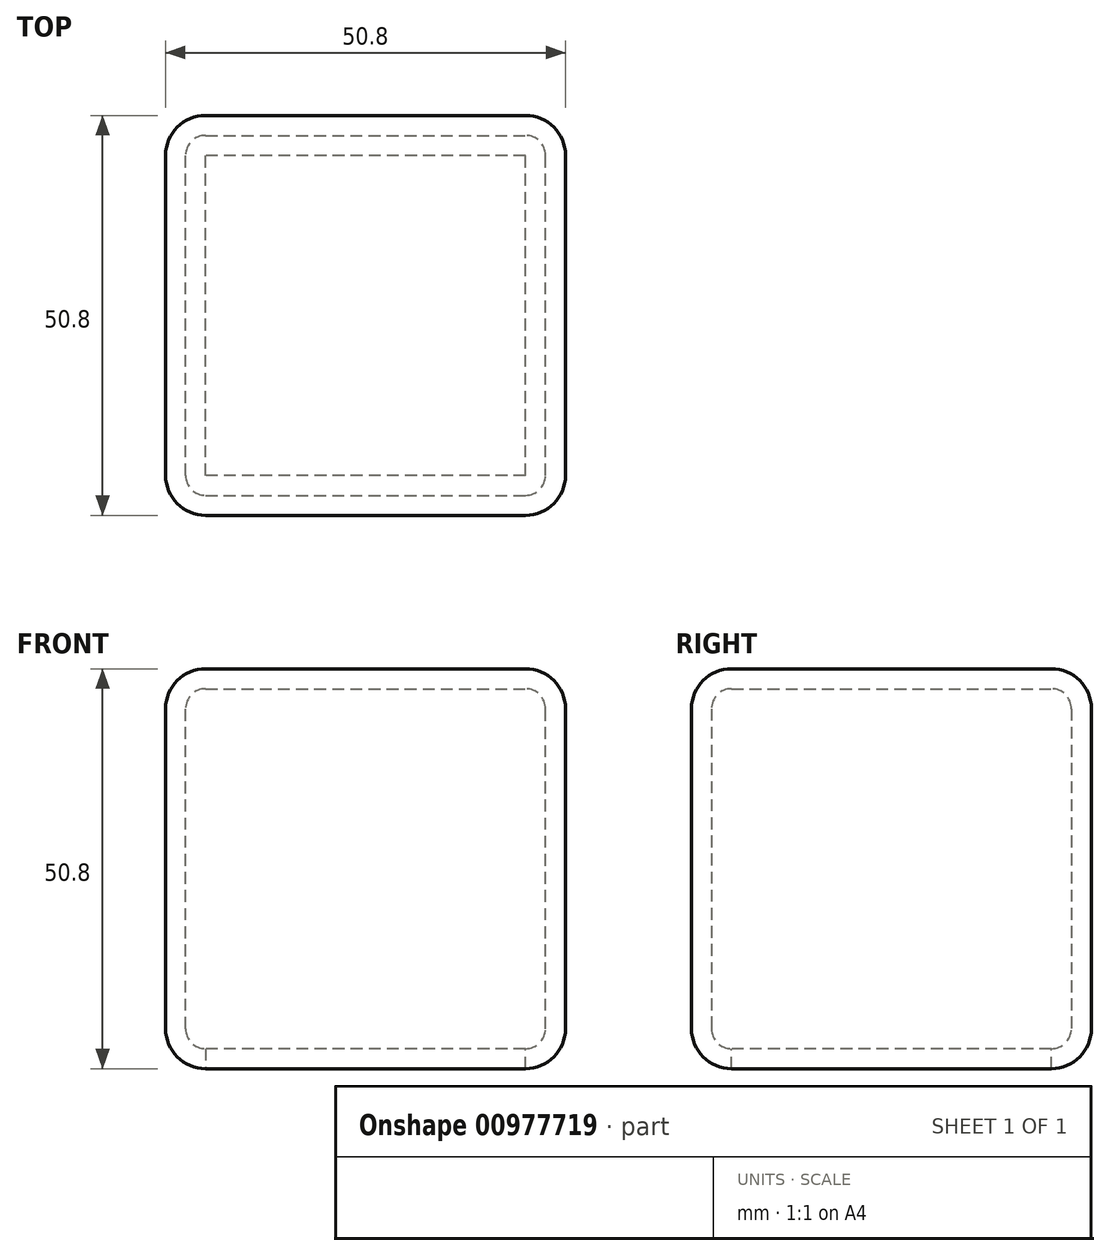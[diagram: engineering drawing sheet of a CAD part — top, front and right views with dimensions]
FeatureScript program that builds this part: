
annotation { "Feature Type Name" : "Feature", "Feature Type Description" : "" }
export const myFeature = defineFeature(function(context is Context, id is Id, definition is map)
    precondition{}
    {
        {
            var Q0;
            Q0=qCreatedBy(makeId("Top.planeOp"),FACE);
            var sketch = newSketch(context, id + "F0", { "sketchPlane" : qUnion([Q0])});
            skLineSegment(sketch, "E0.bottom", {"start": v(25.4, -25.4) * mm, "end": v(-25.4, -25.4) * mm});
            skLineSegment(sketch, "E0.top", {"start": v(25.4, 25.4) * mm, "end": v(-25.4, 25.4) * mm});
            skLineSegment(sketch, "E0.left", {"start": v(25.4, -25.4) * mm, "end": v(25.4, 25.4) * mm});
            skLineSegment(sketch, "E0.right", {"start": v(-25.4, -25.4) * mm, "end": v(-25.4, 25.4) * mm});
            skPoint(sketch, "E0.middle", {"position": v(0, 0) * mm});
            skSolve(sketch);
        }
        {
            var Q0;
            Q0=makeQuery(id+"F0.imprint","IMPRINT",FACE,{"disambiguationData":[TD([[makeQuery(id+"F0.imprint","IMPRINT",EDGE,{"derivedFrom":sQuery(id+"F0.wireOp",EDGE,"E0.bottom")}),-1.0]])]});
            extrude(context, id + "F1", {"entities" : qUnion([Q0]), "depth" : 50.8 * mm, "offsetDistance" : 25.4 * mm});
        }
        {
            var Q0;
            Q0=makeQuery(id+"F1.opExtrude","CAP_EDGE",EDGE,{"disambiguationData":[OSD([sQuery(id+"F0.wireOp",EDGE,"E0.right")])],"isStart":true});
            var Q1;
            Q1=makeQuery(id+"F1.opExtrude","CAP_EDGE",EDGE,{"disambiguationData":[OSD([sQuery(id+"F0.wireOp",EDGE,"E0.right")])],"isStart":false});
            var Q2;
            Q2=makeQuery(id+"F1.opExtrude","SWEPT_EDGE",EDGE,{"disambiguationData":[OSD([sQuery(id+"F0.wireOp",EDGE,"E0.top"),sQuery(id+"F0.wireOp",EDGE,"E0.right")])]});
            var Q3;
            Q3=makeQuery(id+"F1.opExtrude","CAP_EDGE",EDGE,{"disambiguationData":[OSD([sQuery(id+"F0.wireOp",EDGE,"E0.left")])],"isStart":false});
            var Q4;
            Q4=makeQuery(id+"F1.opExtrude","CAP_EDGE",EDGE,{"disambiguationData":[OSD([sQuery(id+"F0.wireOp",EDGE,"E0.top")])],"isStart":false});
            var Q5;
            Q5=makeQuery(id+"F1.opExtrude","CAP_EDGE",EDGE,{"disambiguationData":[OSD([sQuery(id+"F0.wireOp",EDGE,"E0.bottom")])],"isStart":false});
            var Q6;
            Q6=makeQuery(id+"F1.opExtrude","SWEPT_EDGE",EDGE,{"disambiguationData":[OSD([sQuery(id+"F0.wireOp",EDGE,"E0.bottom"),sQuery(id+"F0.wireOp",EDGE,"E0.right")])]});
            var Q7;
            Q7=makeQuery(id+"F1.opExtrude","SWEPT_EDGE",EDGE,{"disambiguationData":[OSD([sQuery(id+"F0.wireOp",EDGE,"E0.top"),sQuery(id+"F0.wireOp",EDGE,"E0.left")])]});
            var Q8;
            Q8=makeQuery(id+"F1.opExtrude","CAP_EDGE",EDGE,{"disambiguationData":[OSD([sQuery(id+"F0.wireOp",EDGE,"E0.top")])],"isStart":true});
            var Q9;
            Q9=makeQuery(id+"F1.opExtrude","CAP_EDGE",EDGE,{"disambiguationData":[OSD([sQuery(id+"F0.wireOp",EDGE,"E0.left")])],"isStart":true});
            var Q10;
            Q10=makeQuery(id+"F1.opExtrude","SWEPT_EDGE",EDGE,{"disambiguationData":[OSD([sQuery(id+"F0.wireOp",EDGE,"E0.bottom"),sQuery(id+"F0.wireOp",EDGE,"E0.left")])]});
            var Q11;
            Q11=makeQuery(id+"F1.opExtrude","CAP_EDGE",EDGE,{"disambiguationData":[OSD([sQuery(id+"F0.wireOp",EDGE,"E0.bottom")])],"isStart":true});
            fillet(context, id + "F2", {"entities" : qUnion([Q0, Q1, Q2, Q3, Q4, Q5, Q6, Q7, Q8, Q9, Q10, Q11]), "radius" : 5.08 * mm, "tangentPropagation" : true, "allowEdgeOverflow" : false});
        }
        {
            var Q0;
            Q0=makeQuery(id+"F1.opExtrude","CAP_FACE",FACE,{"disambiguationData":[OSD([sQuery(id+"F0.wireOp",EDGE,"E0.bottom"),sQuery(id+"F0.wireOp",EDGE,"E0.top"),sQuery(id+"F0.wireOp",EDGE,"E0.left"),sQuery(id+"F0.wireOp",EDGE,"E0.right")])],"isStart":true});
            shell(context, id + "F3", {"entities" : qUnion([Q0]), "thickness" : 2.54 * mm});
        }
    });
